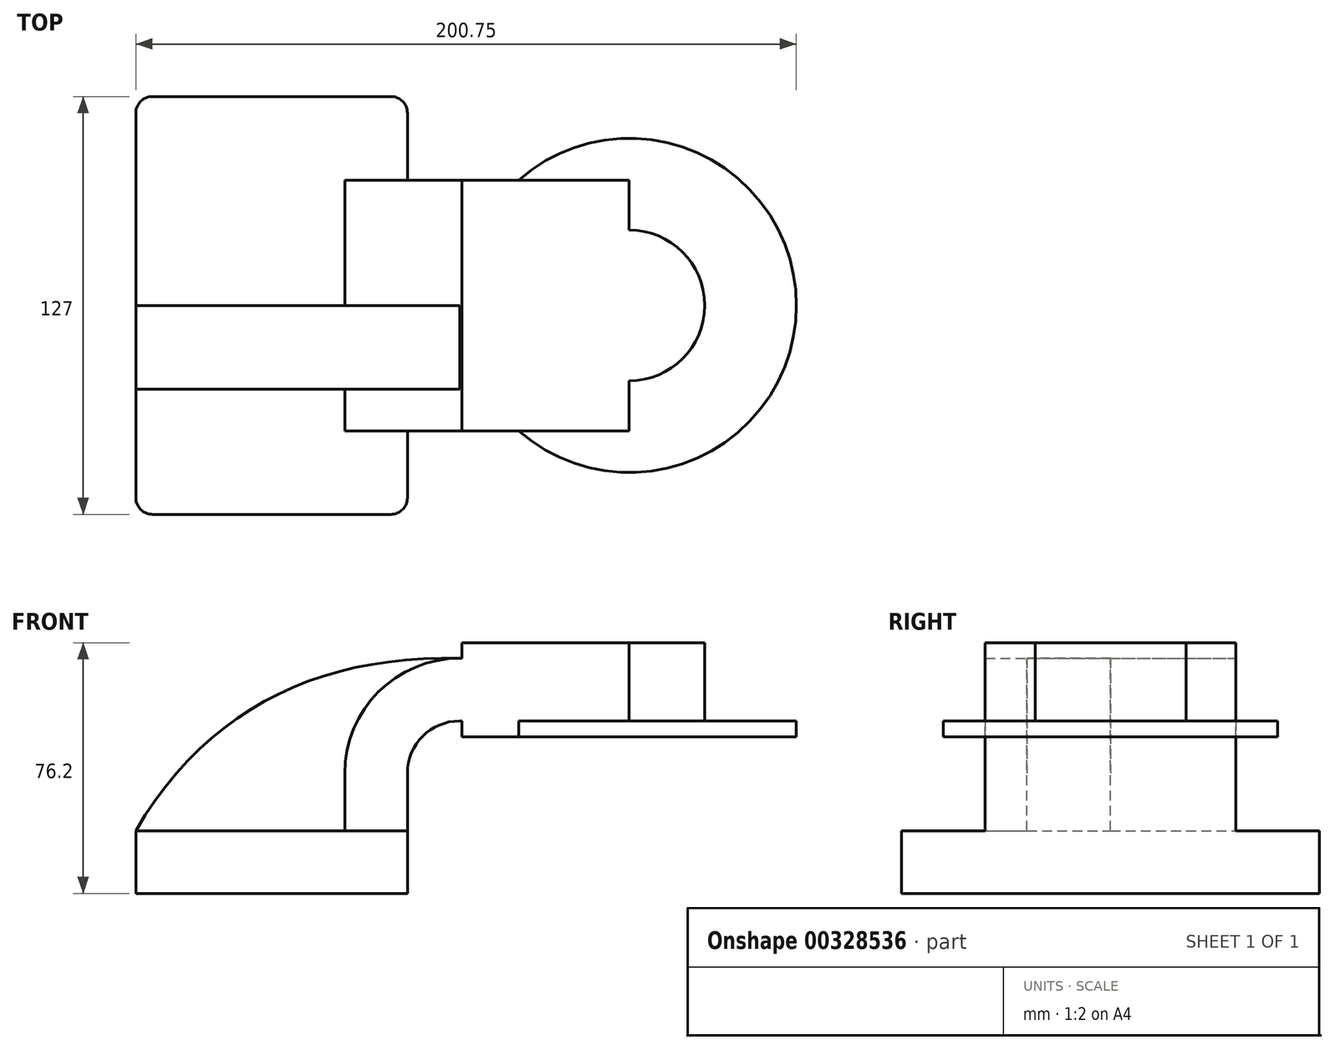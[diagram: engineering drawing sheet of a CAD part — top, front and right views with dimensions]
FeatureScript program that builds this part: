
annotation { "Feature Type Name" : "Feature", "Feature Type Description" : "" }
export const myFeature = defineFeature(function(context is Context, id is Id, definition is map)
    precondition{}
    {
        {
            var Q0;
            Q0=qCreatedBy(makeId("Front.planeOp"),FACE);
            var sketch = newSketch(context, id + "F0", { "sketchPlane" : qUnion([Q0])});
            skLineSegment(sketch, "E0.bottom", {"start": v(-41.28, -9.53) * mm, "end": v(41.28, -9.53) * mm});
            skLineSegment(sketch, "E0.top", {"start": v(-41.28, 9.53) * mm, "end": v(41.28, 9.53) * mm});
            skLineSegment(sketch, "E0.left", {"start": v(-41.28, -9.53) * mm, "end": v(-41.28, 9.53) * mm});
            skLineSegment(sketch, "E0.right", {"start": v(41.28, -9.53) * mm, "end": v(41.28, 9.53) * mm});
            skPoint(sketch, "E0.middle", {"position": v(0, 0) * mm});
            skLineSegment(sketch, "E1.bottom", {"start": v(57.87, 38.1) * mm, "end": v(108.67, 38.1) * mm});
            skLineSegment(sketch, "E1.top", {"start": v(57.87, 66.67) * mm, "end": v(108.67, 66.67) * mm});
            skLineSegment(sketch, "E1.left", {"start": v(57.87, 38.1) * mm, "end": v(57.87, 66.67) * mm});
            skLineSegment(sketch, "E1.right", {"start": v(108.67, 38.1) * mm, "end": v(108.67, 66.67) * mm});
            skPoint(sketch, "E1.middle", {"position": v(83.27, 52.39) * mm});
            skLineSegment(sketch, "E2", {"start": v(41.27, 9.53) * mm, "end": v(41.27, 27) * mm});
            skArc(sketch, "E3", {"start": v(41.27, 27) * mm, "mid": v(45.92, 38.23) * mm, "end": v(57.15, 42.88) * mm});
            skLineSegment(sketch, "E4", {"start": v(57.15, 42.88) * mm, "end": v(85.72, 42.88) * mm});
            skLineSegment(sketch, "E5.0", {"start": v(57.15, 61.93) * mm, "end": v(85.72, 61.93) * mm});
            skArc(sketch, "E5.1", {"start": v(22.23, 27) * mm, "mid": v(32.45, 51.7) * mm, "end": v(57.15, 61.93) * mm});
            skLineSegment(sketch, "E5.2", {"start": v(22.22, 9.53) * mm, "end": v(22.22, 27) * mm});
            skLineSegment(sketch, "E6", {"start": v(85.72, 42.88) * mm, "end": v(85.72, 66.67) * mm});
            skFitSpline(sketch, "E7", {"points": [v(-41.28, 9.52) * mm, v(57.15, 61.93) * mm], "startDerivative": vector(64.7, 110.99) * mm, "endDerivative": vector(129.37, -2.8) * mm});
            skSolve(sketch);
        }
        {
            var Q0;
            Q0=makeQuery(id+"F0.imprint","IMPRINT",FACE,{"disambiguationData":[TD([[makeQuery(id+"F0.imprint","IMPRINT",EDGE,{"derivedFrom":sQuery(id+"F0.wireOp",EDGE,"E0.bottom")}),1.0]])]});
            extrude(context, id + "F1", {"entities" : qUnion([Q0]), "endBound" : BoundingType.SYMMETRIC, "depth" : 127 * mm});
        }
        {
            var Q0;
            Q0=makeQuery(id+"F0.imprint","IMPRINT",FACE,{"disambiguationData":[TD([[makeQuery(id+"F0.imprint","IMPRINT",EDGE,{"derivedFrom":sQuery(id+"F0.wireOp",EDGE,"E5.1")}),1.0]])]});
            extrude(context, id + "F2", {"entities" : qUnion([Q0]), "operationType" : NewBodyOperationType.ADD, "endBound" : BoundingType.SYMMETRIC, "depth" : 50.8 * mm});
        }
        {
            var Q0;
            {var subQ2=sQuery(id+"F0.wireOp",EDGE,"E1.bottom");Q0=makeQuery(id+"F0.imprint","IMPRINT",FACE,{"disambiguationData":[TD([[makeQuery(id+"F0.imprint","IMPRINT",EDGE,{"derivedFrom":subQ2}),1.0]])]});}
            var Q1;
            {var subQ1=sQuery(id+"F0.wireOp",EDGE,"E2");Q1=makeQuery(id+"F0.imprint","IMPRINT",FACE,{"disambiguationData":[TD([[makeQuery(id+"F0.imprint","IMPRINT",EDGE,{"derivedFrom":subQ1}),1.0]])]});}
            var Q2;
            {var subQ0=sQuery(id+"F0.wireOp",EDGE,"E1.left");var subQ1=sQuery(id+"F0.wireOp",EDGE,"E1.top");var subQ2=makeQuery(id+"F0.imprint","INTERSECT",VERTEX,{"derivedFrom":[subQ1,subQ0]});Q2=makeQuery(id+"F0.imprint","IMPRINT",FACE,{"disambiguationData":[TD([[makeQuery(id+"F0.imprint","IMPRINT",EDGE,{"disambiguationData":[TD([[subQ2,-1.0]])],"derivedFrom":subQ1}),-1.0]])]});}
            var Q3;
            {var subQ0=sQuery(id+"F0.wireOp",EDGE,"E4");var subQ1=sQuery(id+"F0.wireOp",EDGE,"E1.left");var subQ2=makeQuery(id+"F0.imprint","INTERSECT",VERTEX,{"derivedFrom":[subQ1,subQ0]});Q3=makeQuery(id+"F0.imprint","IMPRINT",FACE,{"disambiguationData":[TD([[makeQuery(id+"F0.imprint","IMPRINT",EDGE,{"disambiguationData":[TD([[subQ2,-1.0]])],"derivedFrom":subQ1}),-1.0]])]});}
            extrude(context, id + "F3", {"entities" : qUnion([Q0, Q1, Q2, Q3]), "operationType" : NewBodyOperationType.ADD, "endBound" : BoundingType.SYMMETRIC, "depth" : 76.2 * mm});
        }
        {
            var Q0;
            Q0 = qSketchRegion(id + "F0", true);
            extrude(context, id + "F4", {"entities" : qUnion([Q0]), "operationType" : NewBodyOperationType.ADD, "depth" : 25.4 * mm});
        }
        {
            var Q0;
            {var subQ2=sQuery(id+"F0.wireOp",EDGE,"E1.bottom");Q0=makeQuery(id+"F0.imprint","IMPRINT",FACE,{"disambiguationData":[TD([[makeQuery(id+"F0.imprint","IMPRINT",EDGE,{"derivedFrom":subQ2}),1.0]])]});}
            var Q1;
            Q1=sQuery(id+"F0.wireOp",EDGE,"E1.right");
            revolve(context, id + "F5", {"operationType" : NewBodyOperationType.ADD, "entities" : qUnion([Q0]), "axis" : qUnion([Q1]), "revolveType" : RevolveType.FULL});
        }
        {
            var Q0;
            Q0=makeQuery(id+"F1.opExtrude","CAP_EDGE",EDGE,{"disambiguationData":[OSD([sQuery(id+"F0.wireOp",EDGE,"E0.left")])],"isStart":true});
            var Q1;
            Q1=makeQuery(id+"F1.opExtrude","CAP_EDGE",EDGE,{"disambiguationData":[OSD([sQuery(id+"F0.wireOp",EDGE,"E0.right")])],"isStart":true});
            var Q2;
            Q2=makeQuery(id+"F1.opExtrude","CAP_EDGE",EDGE,{"disambiguationData":[OSD([sQuery(id+"F0.wireOp",EDGE,"E0.left")])],"isStart":false});
            var Q3;
            Q3=makeQuery(id+"F1.opExtrude","CAP_EDGE",EDGE,{"disambiguationData":[OSD([sQuery(id+"F0.wireOp",EDGE,"E0.right")])],"isStart":false});
            fillet(context, id + "F6", {"entities" : qUnion([Q0, Q1, Q2, Q3]), "radius" : 5.08 * mm, "tangentPropagation" : true, "allowEdgeOverflow" : false});
        }
    });
